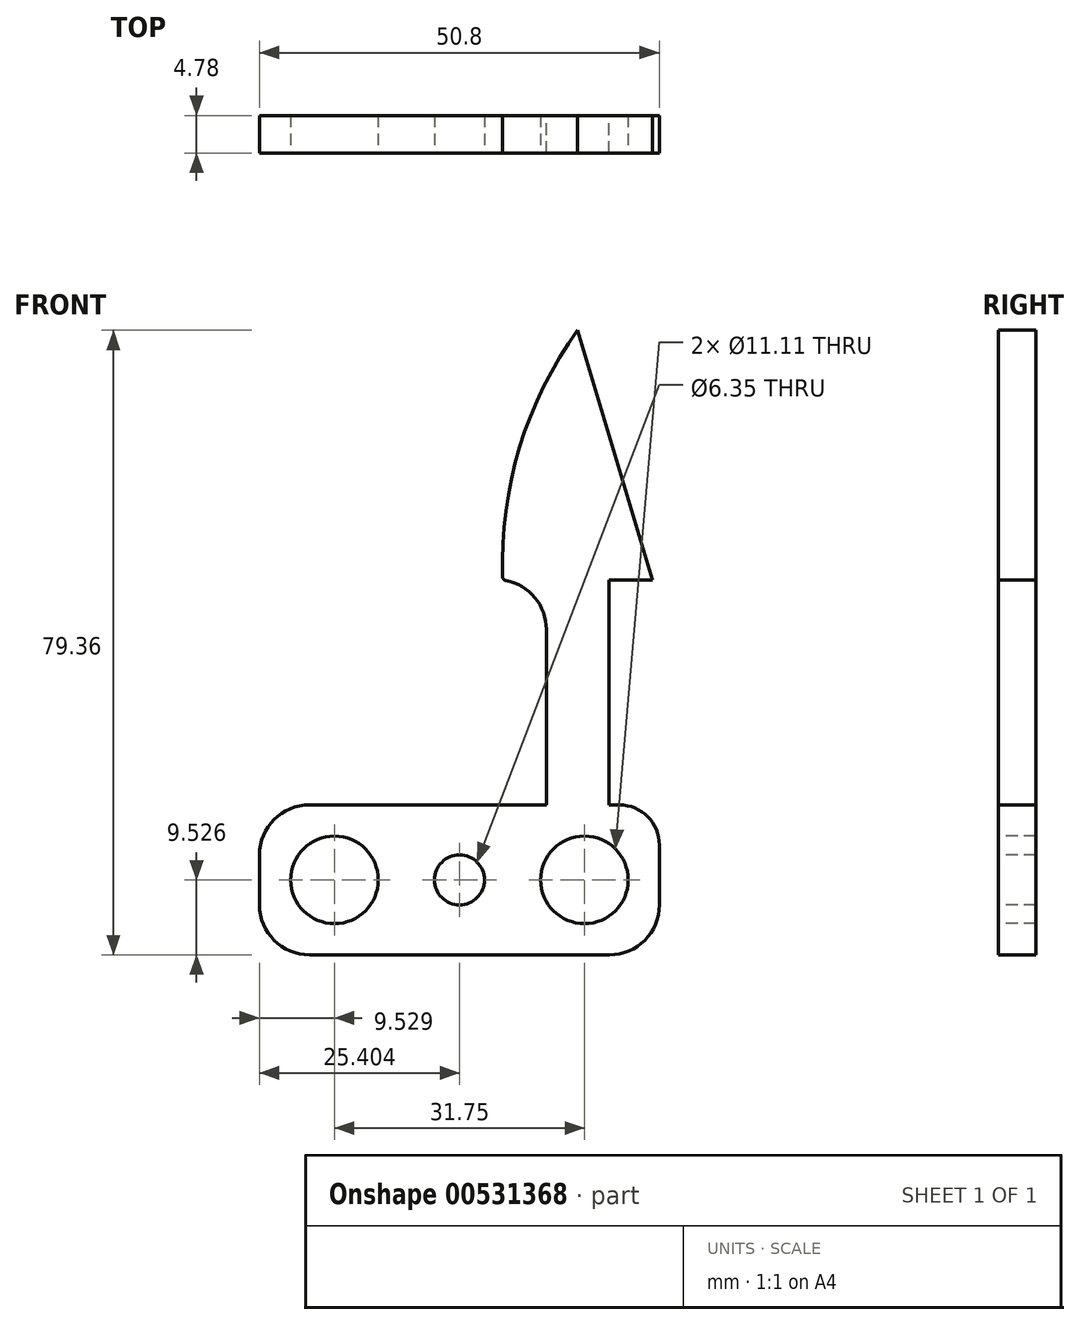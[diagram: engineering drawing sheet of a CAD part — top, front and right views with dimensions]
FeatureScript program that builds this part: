
annotation { "Feature Type Name" : "Feature", "Feature Type Description" : "" }
export const myFeature = defineFeature(function(context is Context, id is Id, definition is map)
    precondition{}
    {
        {
            var Q0;
            Q0=qCreatedBy(makeId("Front.planeOp"),FACE);
            var sketch = newSketch(context, id + "F0", { "sketchPlane" : qUnion([Q0])});
            skLineSegment(sketch, "E0.bottom", {"start": v(-31.8, 11.48) * mm, "end": v(19, 11.48) * mm});
            skLineSegment(sketch, "E0.top", {"start": v(-31.8, -7.57) * mm, "end": v(19, -7.57) * mm});
            skLineSegment(sketch, "E0.left", {"start": v(-31.8, 11.48) * mm, "end": v(-31.8, -7.57) * mm});
            skLineSegment(sketch, "E0.right", {"start": v(19, 11.48) * mm, "end": v(19, -7.57) * mm});
            skSolve(sketch);
        }
        {
            var Q0;
            Q0=makeQuery(id+"F0.imprint","IMPRINT",FACE,{"disambiguationData":[TD([[makeQuery(id+"F0.imprint","IMPRINT",EDGE,{"derivedFrom":sQuery(id+"F0.wireOp",EDGE,"E0.bottom")}),-1.0]])]});
            var sketch = newSketch(context, id + "F1", { "sketchPlane" : qUnion([Q0])});
            skSolve(sketch);
        }
        {
            var Q0;
            Q0 = qSketchRegion(id + "F1", true);
            var Q1;
            Q1=makeQuery(id+"F1.imprint","IMPRINT",FACE,{"disambiguationData":[TD([[makeQuery(id+"F1.imprint","IMPRINT",EDGE,{"derivedFrom":makeQuery(id+"F0.imprint","IMPRINT",EDGE,{"derivedFrom":sQuery(id+"F0.wireOp",EDGE,"E0.bottom")})}),-1.0]])]});
            extrude(context, id + "F2", {"entities" : qUnion([Q0, Q1]), "depth" : 2.4 * mm, "offsetDistance" : 25.4 * mm, "hasSecondDirection" : true, "secondDirectionOppositeDirection" : true, "secondDirectionDepth" : 2.4 * mm});
        }
        {
            var Q0;
            Q0=makeQuery(id+"F2.opExtrude","SWEPT_EDGE",EDGE,{"disambiguationData":[OSD([sQuery(id+"F0.wireOp",EDGE,"E0.bottom"),sQuery(id+"F0.wireOp",EDGE,"E0.right")])]});
            fillet(context, id + "F3", {"entities" : qUnion([Q0]), "radius" : 5.08 * mm, "tangentPropagation" : true, "allowEdgeOverflow" : false});
        }
        {
            var Q0;
            Q0=makeQuery(id+"F2.opExtrude","SWEPT_EDGE",EDGE,{"disambiguationData":[OSD([sQuery(id+"F0.wireOp",EDGE,"E0.top"),sQuery(id+"F0.wireOp",EDGE,"E0.right")])]});
            fillet(context, id + "F4", {"entities" : qUnion([Q0]), "radius" : 6.35 * mm, "tangentPropagation" : true, "allowEdgeOverflow" : false});
        }
        {
            var Q0;
            Q0=makeQuery(id+"F2.opExtrude","SWEPT_EDGE",EDGE,{"disambiguationData":[OSD([sQuery(id+"F0.wireOp",EDGE,"E0.bottom"),sQuery(id+"F0.wireOp",EDGE,"E0.left")])]});
            var Q1;
            Q1=makeQuery(id+"F2.opExtrude","SWEPT_EDGE",EDGE,{"disambiguationData":[OSD([sQuery(id+"F0.wireOp",EDGE,"E0.top"),sQuery(id+"F0.wireOp",EDGE,"E0.left")])]});
            fillet(context, id + "F5", {"entities" : qUnion([Q0, Q1]), "radius" : 6.35 * mm, "tangentPropagation" : true, "allowEdgeOverflow" : false});
        }
        {
            var Q0;
            Q0=makeQuery(id+"F2.opExtrude","CAP_FACE",FACE,{"disambiguationData":[OSD([sQuery(id+"F0.wireOp",EDGE,"E0.bottom"),sQuery(id+"F0.wireOp",EDGE,"E0.top"),sQuery(id+"F0.wireOp",EDGE,"E0.left"),sQuery(id+"F0.wireOp",EDGE,"E0.right")])],"isStart":false});
            var sketch = newSketch(context, id + "F6", { "sketchPlane" : qUnion([Q0])});
            skPoint(sketch, "E1", {"position": v(9.47, 1.96) * mm});
            skSolve(sketch);
        }
        {
            var Q0;
            Q0=sQuery(id+"F6.wireOp",VERTEX,"E1");
            var Q1;
            Q1=makeQuery(id+"F2.opExtrude","SWEPT_BODY",BODY,{"disambiguationData":[OSD([sQuery(id+"F0.wireOp",EDGE,"E0.bottom"),sQuery(id+"F0.wireOp",EDGE,"E0.top"),sQuery(id+"F0.wireOp",EDGE,"E0.left"),sQuery(id+"F0.wireOp",EDGE,"E0.right")])]});
            hole(context, id + "F7", {"style" : HoleStyle.SIMPLE, "endStyle" : HoleEndStyle.THROUGH, "holeDiameter" : 11.1 * mm, "isTappedThrough" : true, "tappedDepth" : 12.7 * mm, "tapClearance" : 3, "locations" : qUnion([Q0]), "scope" : qUnion([Q1])});
        }
        {
            var Q0;
            Q0=makeQuery(id+"F2.opExtrude","CAP_FACE",FACE,{"disambiguationData":[OSD([sQuery(id+"F0.wireOp",EDGE,"E0.bottom"),sQuery(id+"F0.wireOp",EDGE,"E0.top"),sQuery(id+"F0.wireOp",EDGE,"E0.left"),sQuery(id+"F0.wireOp",EDGE,"E0.right")])],"isStart":false});
            var sketch = newSketch(context, id + "F8", { "sketchPlane" : qUnion([Q0])});
            skPoint(sketch, "E2", {"position": v(-22.28, 1.96) * mm});
            skSolve(sketch);
        }
        {
            var Q0;
            Q0=sQuery(id+"F8.wireOp",VERTEX,"E2");
            var Q1;
            Q1=makeQuery(id+"F2.opExtrude","SWEPT_BODY",BODY,{"disambiguationData":[OSD([sQuery(id+"F0.wireOp",EDGE,"E0.bottom"),sQuery(id+"F0.wireOp",EDGE,"E0.top"),sQuery(id+"F0.wireOp",EDGE,"E0.left"),sQuery(id+"F0.wireOp",EDGE,"E0.right")])]});
            hole(context, id + "F9", {"style" : HoleStyle.SIMPLE, "endStyle" : HoleEndStyle.THROUGH, "holeDiameter" : 11.1 * mm, "isTappedThrough" : true, "tappedDepth" : 12.7 * mm, "tapClearance" : 3, "locations" : qUnion([Q0]), "scope" : qUnion([Q1])});
        }
        {
            var Q0;
            Q0=makeQuery(id+"F2.opExtrude","CAP_FACE",FACE,{"disambiguationData":[OSD([sQuery(id+"F0.wireOp",EDGE,"E0.bottom"),sQuery(id+"F0.wireOp",EDGE,"E0.top"),sQuery(id+"F0.wireOp",EDGE,"E0.left"),sQuery(id+"F0.wireOp",EDGE,"E0.right")])],"isStart":false});
            var sketch = newSketch(context, id + "F10", { "sketchPlane" : qUnion([Q0])});
            skPoint(sketch, "E3", {"position": v(-6.4, 1.96) * mm});
            skSolve(sketch);
        }
        {
            var Q0;
            Q0=sQuery(id+"F10.wireOp",VERTEX,"E3");
            var Q1;
            Q1=makeQuery(id+"F2.opExtrude","SWEPT_BODY",BODY,{"disambiguationData":[OSD([sQuery(id+"F0.wireOp",EDGE,"E0.bottom"),sQuery(id+"F0.wireOp",EDGE,"E0.top"),sQuery(id+"F0.wireOp",EDGE,"E0.left"),sQuery(id+"F0.wireOp",EDGE,"E0.right")])]});
            hole(context, id + "F11", {"style" : HoleStyle.SIMPLE, "endStyle" : HoleEndStyle.THROUGH, "holeDiameter" : 6.35 * mm, "isTappedThrough" : true, "tappedDepth" : 12.7 * mm, "tapClearance" : 3, "locations" : qUnion([Q0]), "scope" : qUnion([Q1])});
        }
        {
            var Q0;
            Q0=qCreatedBy(makeId("Front.planeOp"),FACE);
            var sketch = newSketch(context, id + "F12", { "sketchPlane" : qUnion([Q0])});
            skLineSegment(sketch, "E4.bottom", {"start": v(4.64, 40.04) * mm, "end": v(8.6, 40.04) * mm});
            skLineSegment(sketch, "E4.top", {"start": v(4.64, 11.47) * mm, "end": v(12.57, 11.47) * mm});
            skLineSegment(sketch, "E4.left", {"start": v(4.64, 40.04) * mm, "end": v(4.64, 11.47) * mm});
            skLineSegment(sketch, "E4.right", {"start": v(12.57, 40.04) * mm, "end": v(12.57, 11.47) * mm});
            skLineSegment(sketch, "E5", {"start": v(8.6, 40.04) * mm, "end": v(12.57, 40.04) * mm});
            skSolve(sketch);
        }
        {
            var Q0;
            Q0=makeQuery(id+"F12.imprint","IMPRINT",FACE,{"disambiguationData":[TD([[makeQuery(id+"F12.imprint","IMPRINT",EDGE,{"derivedFrom":sQuery(id+"F12.wireOp",EDGE,"E4.bottom")}),-1.0]])]});
            extrude(context, id + "F13", {"entities" : qUnion([Q0]), "operationType" : NewBodyOperationType.ADD, "depth" : 2.4 * mm, "offsetDistance" : 25.4 * mm, "hasSecondDirection" : true, "secondDirectionOppositeDirection" : true, "secondDirectionDepth" : 2.4 * mm});
        }
        {
            var Q0;
            Q0=qCreatedBy(makeId("Front.planeOp"),FACE);
            var sketch = newSketch(context, id + "F14", { "sketchPlane" : qUnion([Q0])});
            skLineSegment(sketch, "E6", {"start": v(8.6, 71.8) * mm, "end": v(18.13, 40.04) * mm});
            skLineSegment(sketch, "E7", {"start": v(18.13, 40.04) * mm, "end": v(8.6, 40.04) * mm});
            skArc(sketch, "E8", {"start": v(8.6, 71.8) * mm, "mid": v(1.18, 56.72) * mm, "end": v(-0.92, 40.04) * mm});
            skLineSegment(sketch, "E9", {"start": v(8.6, 40.04) * mm, "end": v(-0.92, 40.04) * mm});
            skSolve(sketch);
        }
        {
            var Q0;
            Q0 = qSketchRegion(id + "F14", true);
            extrude(context, id + "F15", {"entities" : qUnion([Q0]), "operationType" : NewBodyOperationType.ADD, "depth" : 2.4 * mm, "offsetDistance" : 25.4 * mm, "hasSecondDirection" : true, "secondDirectionOppositeDirection" : true, "secondDirectionDepth" : 2.4 * mm});
        }
        {
            var Q0;
            Q0=makeQuery(id+"F13.opExtrude","SWEPT_EDGE",EDGE,{"disambiguationData":[OSD([sQuery(id+"F12.wireOp",EDGE,"E4.right"),sQuery(id+"F12.wireOp",EDGE,"E5")])]});
            var Q1;
            Q1=makeQuery(id+"F13.opExtrude","SWEPT_EDGE",EDGE,{"disambiguationData":[OSD([sQuery(id+"F12.wireOp",EDGE,"E4.bottom"),sQuery(id+"F12.wireOp",EDGE,"E4.left")])]});
            fillet(context, id + "F16", {"entities" : qUnion([Q0, Q1]), "radius" : 6.35 * mm, "tangentPropagation" : true, "allowEdgeOverflow" : false});
        }
        {
            var Q0;
            Q0=makeQuery(id+"F16.opFillet","BLEND_EDGE",EDGE,{"blendedFrom":[makeQuery(id+"F13.opExtrude","SWEPT_EDGE",EDGE,{"disambiguationData":[OSD([sQuery(id+"F12.wireOp",EDGE,"E4.right"),sQuery(id+"F12.wireOp",EDGE,"E5")])]}),makeQuery(id+"F15.opExtrude","SWEPT_FACE",FACE,{"disambiguationData":[OSD([sQuery(id+"F14.wireOp",EDGE,"E6")])]})],"blendedInto":[makeQuery(id+"F15.opExtrude","SWEPT_FACE",FACE,{"disambiguationData":[OSD([sQuery(id+"F14.wireOp",EDGE,"E6")])]})]});
            var Q1;
            Q1=makeQuery(id+"F16.opFillet","BLEND_EDGE",EDGE,{"blendedFrom":[makeQuery(id+"F13.opExtrude","SWEPT_EDGE",EDGE,{"disambiguationData":[OSD([sQuery(id+"F12.wireOp",EDGE,"E4.bottom"),sQuery(id+"F12.wireOp",EDGE,"E4.left")])]}),makeQuery(id+"F15.opExtrude","SWEPT_FACE",FACE,{"disambiguationData":[OSD([sQuery(id+"F14.wireOp",EDGE,"E8")])]})],"blendedInto":[makeQuery(id+"F15.opExtrude","SWEPT_FACE",FACE,{"disambiguationData":[OSD([sQuery(id+"F14.wireOp",EDGE,"E8")])]})]});
            fillet(context, id + "F17", {"entities" : qUnion([Q0, Q1]), "radius" : 0.5 * mm, "tangentPropagation" : true, "allowEdgeOverflow" : false});
        }
    });
